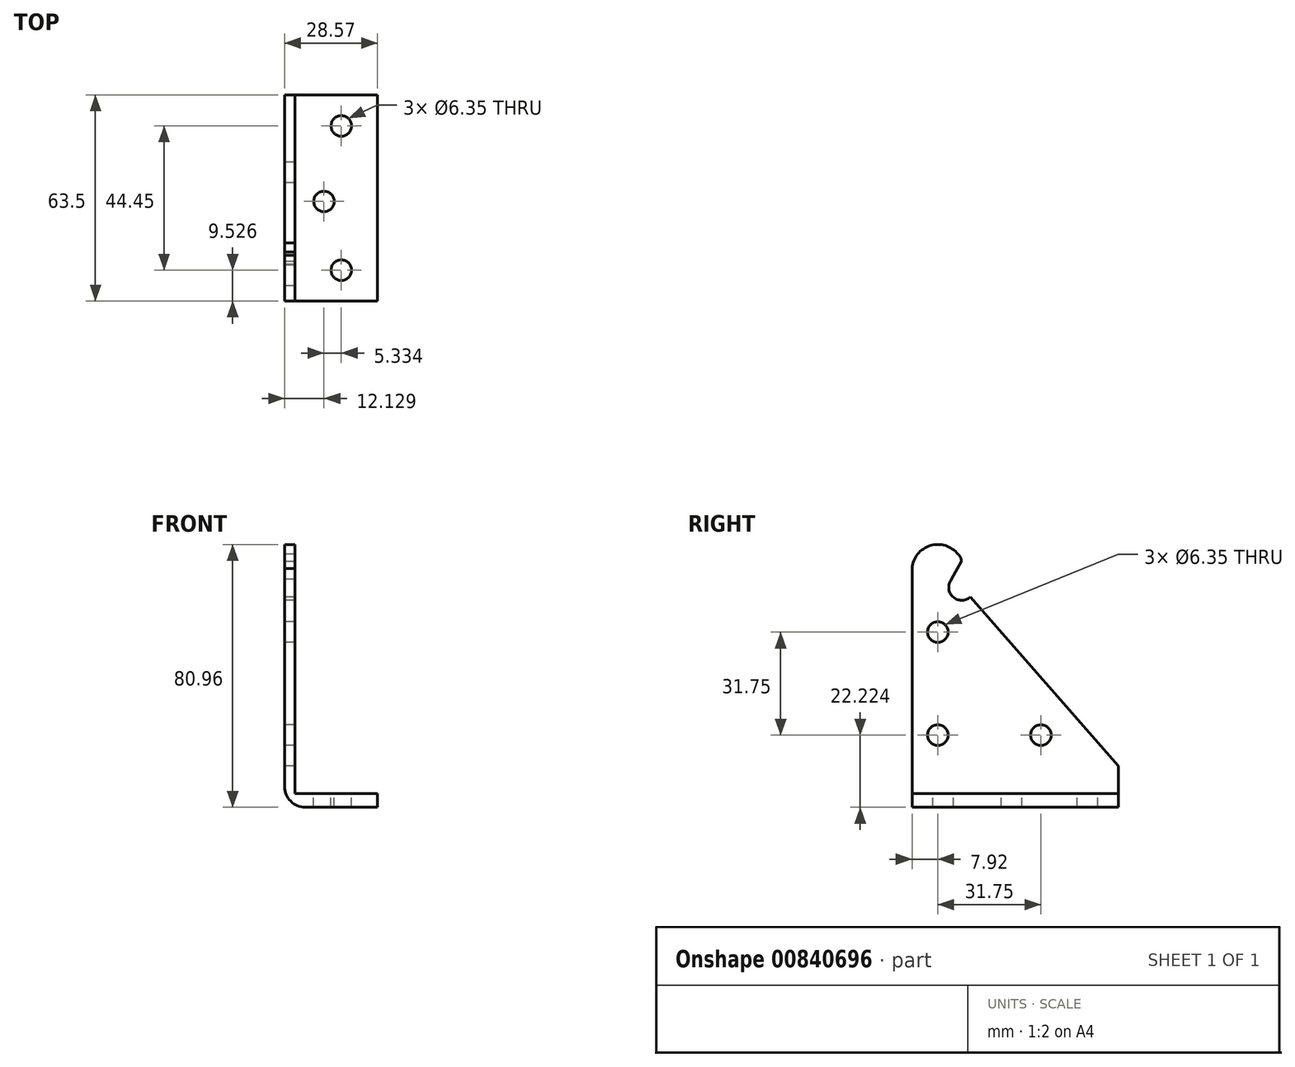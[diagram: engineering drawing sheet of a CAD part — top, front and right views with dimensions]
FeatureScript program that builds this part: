
annotation { "Feature Type Name" : "Feature", "Feature Type Description" : "" }
export const myFeature = defineFeature(function(context is Context, id is Id, definition is map)
    precondition{}
    {
        {
            var Q0;
            Q0=qCreatedBy(makeId("Right.planeOp"),FACE);
            var sketch = newSketch(context, id + "F0", { "sketchPlane" : qUnion([Q0])});
            skArc(sketch, "E0", {"start": v(-18.7, 20.27) * mm, "mid": v(-27.27, 22.95) * mm, "end": v(-32.86, 15.92) * mm});
            skArc(sketch, "E1", {"start": v(-17.73, 18.1) * mm, "mid": v(-17.95, 19.3) * mm, "end": v(-18.7, 20.27) * mm});
            skCircle(sketch, "E2", {"center": v(-24.94, -3.69) * mm, "radius": 3.18 * mm});
            skLineSegment(sketch, "E3", {"start": v(-32.86, 15.92) * mm, "end": v(-32.86, -57.66) * mm});
            skCircle(sketch, "E4", {"center": v(-24.94, -35.44) * mm, "radius": 3.18 * mm});
            skLineSegment(sketch, "E5", {"start": v(-32.86, -57.66) * mm, "end": v(30.64, -57.66) * mm});
            skLineSegment(sketch, "E6", {"start": v(30.64, -57.66) * mm, "end": v(30.64, -44.96) * mm});
            skLineSegment(sketch, "E7", {"start": v(-17.73, 18.1) * mm, "end": v(-20.7, 12.57) * mm});
            skArc(sketch, "E8", {"start": v(-20.7, 12.57) * mm, "mid": v(-20.34, 7.2) * mm, "end": v(-14.97, 7.12) * mm});
            skLineSegment(sketch, "E9", {"start": v(-14.97, 7.12) * mm, "end": v(30.64, -44.96) * mm});
            skCircle(sketch, "E10", {"center": v(6.8, -35.44) * mm, "radius": 3.18 * mm});
            skSolve(sketch);
        }
        {
            var Q0;
            Q0=makeQuery(id+"F0.imprint","IMPRINT",FACE,{"disambiguationData":[TD([[makeQuery(id+"F0.imprint","IMPRINT",EDGE,{"derivedFrom":sQuery(id+"F0.wireOp",EDGE,"E0")}),1.0]])]});
            extrude(context, id + "F1", {"entities" : qUnion([Q0]), "depth" : 3.17 * mm, "offsetDistance" : 25.4 * mm});
        }
        {
            var Q0;
            Q0=makeQuery(id+"F1.opExtrude","CAP_FACE",FACE,{"disambiguationData":[OSD([sQuery(id+"F0.wireOp",EDGE,"E0"),sQuery(id+"F0.wireOp",EDGE,"E1"),sQuery(id+"F0.wireOp",EDGE,"E2"),sQuery(id+"F0.wireOp",EDGE,"E3"),sQuery(id+"F0.wireOp",EDGE,"E4"),sQuery(id+"F0.wireOp",EDGE,"E5"),sQuery(id+"F0.wireOp",EDGE,"E6"),sQuery(id+"F0.wireOp",EDGE,"E7"),sQuery(id+"F0.wireOp",EDGE,"E8"),sQuery(id+"F0.wireOp",EDGE,"E9"),sQuery(id+"F0.wireOp",EDGE,"E10")])],"isStart":false});
            var sketch = newSketch(context, id + "F2", { "sketchPlane" : qUnion([Q0])});
            skLineSegment(sketch, "E11.bottom", {"start": v(-32.86, -57.66) * mm, "end": v(30.64, -57.66) * mm});
            skLineSegment(sketch, "E11.top", {"start": v(-32.86, -53.47) * mm, "end": v(30.64, -53.47) * mm});
            skLineSegment(sketch, "E11.left", {"start": v(-32.86, -57.66) * mm, "end": v(-32.86, -53.47) * mm});
            skLineSegment(sketch, "E11.right", {"start": v(30.64, -57.66) * mm, "end": v(30.64, -53.47) * mm});
            skSolve(sketch);
        }
        {
            var Q0;
            Q0 = qSketchRegion(id + "F2", true);
            extrude(context, id + "F3", {"entities" : qUnion([Q0]), "operationType" : NewBodyOperationType.ADD, "depth" : 25.4 * mm, "offsetDistance" : 25.4 * mm});
        }
        {
            var Q0;
            Q0=makeQuery(id+"F3.opExtrude","SWEPT_FACE",FACE,{"disambiguationData":[OSD([sQuery(id+"F2.wireOp",EDGE,"E11.top")])]});
            var sketch = newSketch(context, id + "F4", { "sketchPlane" : qUnion([Q0])});
            skCircle(sketch, "E12", {"center": v(17.46, -23.33) * mm, "radius": 3.18 * mm});
            skCircle(sketch, "E13", {"center": v(17.46, 21.12) * mm, "radius": 3.18 * mm});
            skCircle(sketch, "E14", {"center": v(12.13, -2.16) * mm, "radius": 3.18 * mm});
            skSolve(sketch);
        }
        {
            var Q0;
            Q0 = qSketchRegion(id + "F4", true);
            extrude(context, id + "F5", {"entities" : qUnion([Q0]), "operationType" : NewBodyOperationType.REMOVE, "oppositeDirection" : true, "depth" : 25.4 * mm, "offsetDistance" : 25.4 * mm});
        }
        {
            var Q0;
            Q0=makeQuery(id+"F3.opExtrude","CAP_EDGE",EDGE,{"disambiguationData":[OSD([sQuery(id+"F2.wireOp",EDGE,"E11.top")])],"isStart":true});
            var Q1;
            Q1=makeQuery(id+"F1.opExtrude","CAP_EDGE",EDGE,{"disambiguationData":[OSD([sQuery(id+"F0.wireOp",EDGE,"E5")])],"isStart":true});
            fillet(context, id + "F6", {"entities" : qUnion([Q0, Q1]), "radius" : 6.35 * mm, "tangentPropagation" : true, "allowEdgeOverflow" : false});
        }
    });
